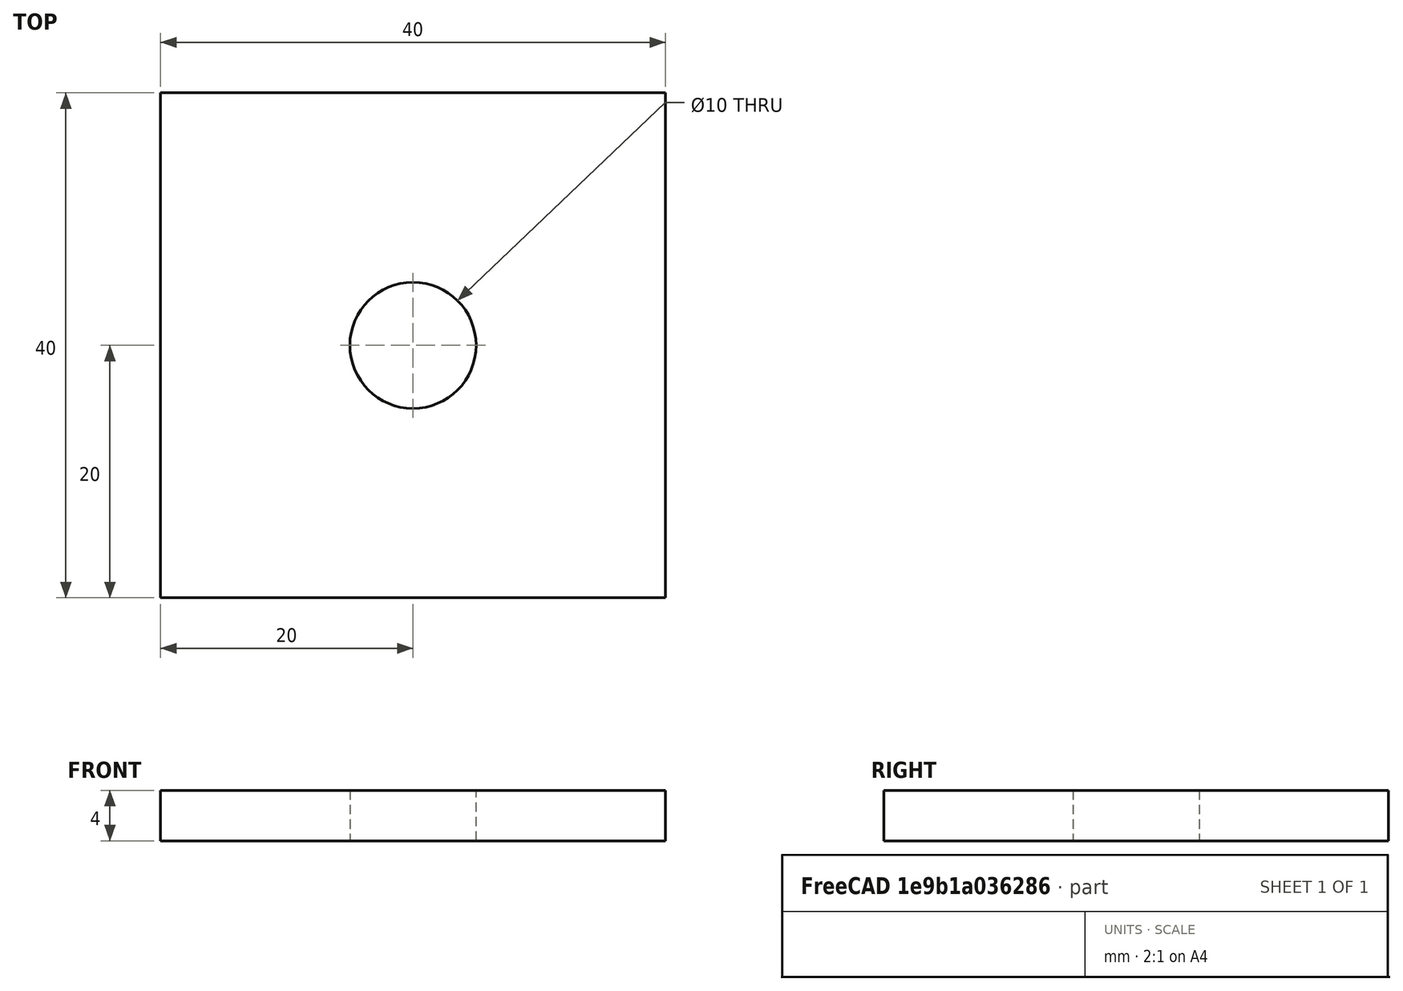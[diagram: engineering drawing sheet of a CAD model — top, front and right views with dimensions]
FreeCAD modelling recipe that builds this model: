
FCSTD DOCUMENT  (FreeCAD 0.20R29410 (Git))
Label: cuadrado_taladro
License: Creative Commons Attribution
LicenseURL: http://creativecommons.org/licenses/by/4.0/
objects: Sketcher::SketchObject×1, Part::Extrusion×1
note: 2 computed .brp shape members not serialized (recipe doc carries the construction recipe); baked Part::Feature solids carry a one-line shape summary decoded from their .brp

FEATURE [Sketcher::SketchObject] Sketch  label="plano_cuad_taladro"
  FullyConstrained = true
  sketch-geometry (5):
    g0: LineSegment StartX=-20 StartY=20 StartZ=0 EndX=20 EndY=20 EndZ=0
    g1: LineSegment StartX=20 StartY=20 StartZ=0 EndX=20 EndY=-20 EndZ=0
    g2: LineSegment StartX=20 StartY=-20 StartZ=0 EndX=-20 EndY=-20 EndZ=0
    g3: LineSegment StartX=-20 StartY=-20 StartZ=0 EndX=-20 EndY=20 EndZ=0
    g4: Circle CenterX=0 CenterY=0 CenterZ=0 NormalX=0 NormalY=0 NormalZ=1 AngleXU=0 Radius=5
  constraints (13):
    c: Coincident(g0,g1)
    c: Coincident(g1,g2)
    c: Coincident(g2,g3)
    c: Coincident(g3,g0)
    c: Horizontal(g0)
    c: Horizontal(g2)
    c: Vertical(g1)
    c: Vertical(g3)
    c: Symmetric(g0,g1,g-1)
    c: Equal(g0,g1)
    c: DistanceX(g0,g0) = 40  'Lado'
    c: Coincident(g4,g-1)
    c: Diameter(g4) = 10  'Diametro'
FEATURE [Part::Extrusion] Extrude
  Base = -> Sketch
  Dir = (0,0,1)
  DirMode = 2
  FaceMakerClass = Part::FaceMakerBullseye
  LengthFwd = 4
  LengthRev = 0
  Solid = true
  Symmetric = false
